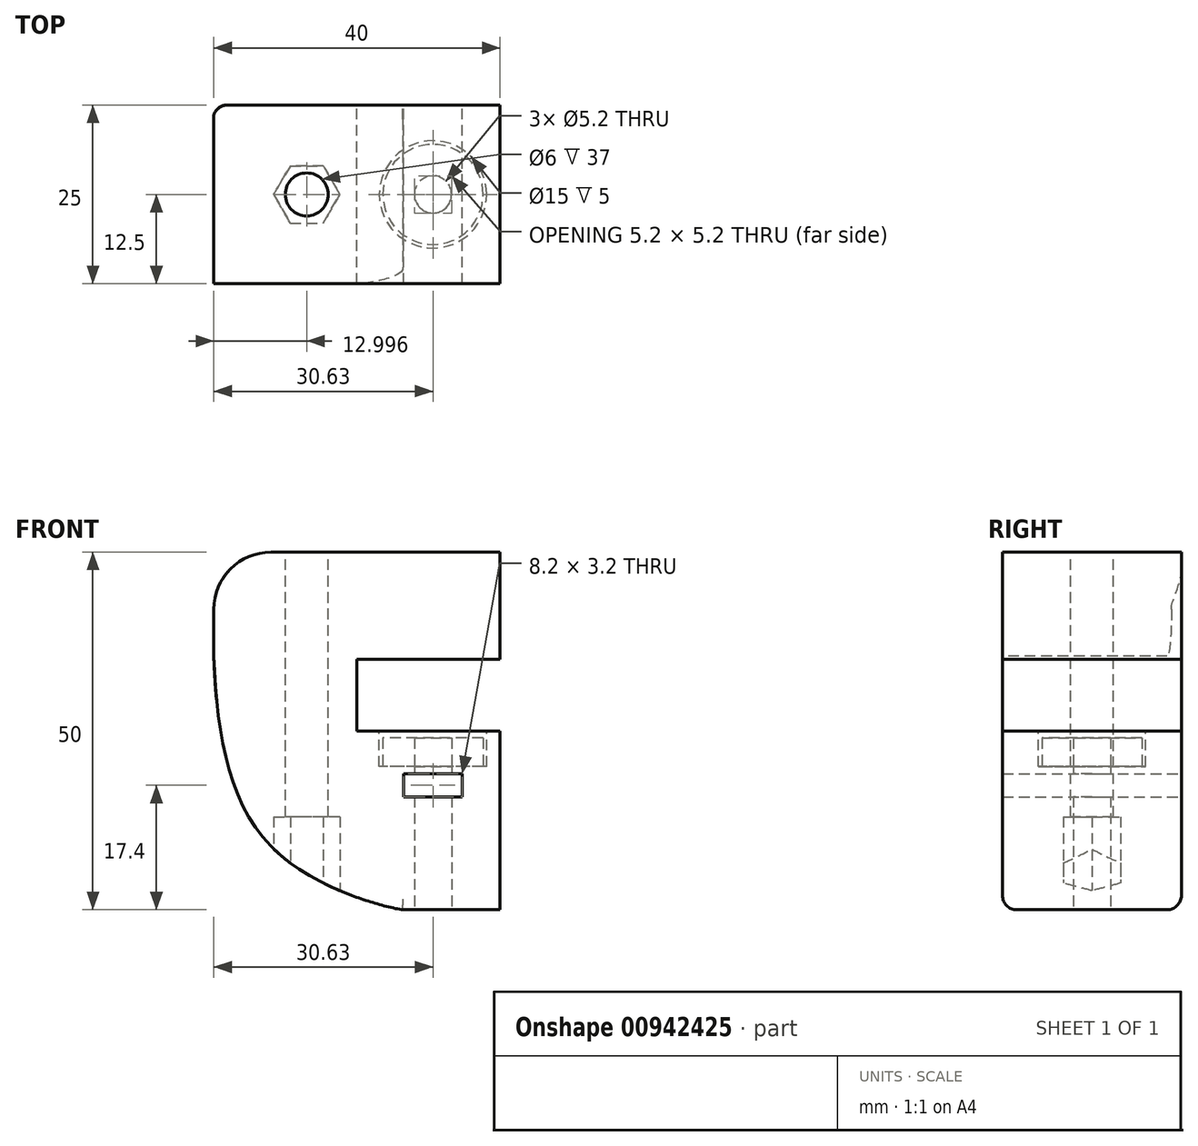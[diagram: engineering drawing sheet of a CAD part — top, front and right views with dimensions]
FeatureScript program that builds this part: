
annotation { "Feature Type Name" : "Feature", "Feature Type Description" : "" }
export const myFeature = defineFeature(function(context is Context, id is Id, definition is map)
    precondition{}
    {
        {
            var Q0;
            Q0=qCreatedBy(makeId("Front.planeOp"),FACE);
            var sketch = newSketch(context, id + "F0", { "sketchPlane" : qUnion([Q0])});
            skLineSegment(sketch, "E0", {"start": v(9.37, 10) * mm, "end": v(9.37, 25) * mm});
            skLineSegment(sketch, "E1", {"start": v(9.37, 25) * mm, "end": v(-30.63, 25) * mm});
            skLineSegment(sketch, "E2", {"start": v(-30.63, 25) * mm, "end": v(-30.63, -25) * mm});
            skLineSegment(sketch, "E3", {"start": v(9.37, -25) * mm, "end": v(9.37, 0) * mm});
            skLineSegment(sketch, "E4", {"start": v(-30.63, -25) * mm, "end": v(9.37, -25) * mm});
            skLineSegment(sketch, "E5", {"start": v(9.37, 10) * mm, "end": v(-10.63, 10) * mm});
            skLineSegment(sketch, "E6", {"start": v(-10.63, 10) * mm, "end": v(-10.63, 0) * mm});
            skLineSegment(sketch, "E7", {"start": v(-10.63, 0) * mm, "end": v(9.37, 0) * mm});
            skLineSegment(sketch, "E8.bottom", {"start": v(-4.1, -6) * mm, "end": v(4.1, -6) * mm});
            skLineSegment(sketch, "E8.top", {"start": v(-4.1, -9.2) * mm, "end": v(4.1, -9.2) * mm});
            skLineSegment(sketch, "E8.left", {"start": v(-4.1, -6) * mm, "end": v(-4.1, -9.2) * mm});
            skLineSegment(sketch, "E8.right", {"start": v(4.1, -6) * mm, "end": v(4.1, -9.2) * mm});
            skFitSpline(sketch, "E9", {"points": [v(-25, 25) * mm, v(-21.25, -15.4) * mm, v(9.37, -19.87) * mm], "startDerivative": vector(2.03, -83.34) * mm, "endDerivative": vector(87.72, 0.68) * mm});
            skSolve(sketch);
        }
        {
            var Q0;
            Q0=qSketchRegion(id+"F0",true);
            extrude(context, id + "F1", {"entities" : qUnion([Q0]), "depth" : 25 * mm, "offsetDistance" : 25 * mm});
        }
        {
            var Q0;
            Q0=makeQuery(id+"F1.opExtrude","SWEPT_FACE",FACE,{"disambiguationData":[OSD([sQuery(id+"F0.wireOp",EDGE,"E1")])]});
            var sketch = newSketch(context, id + "F2", { "sketchPlane" : qUnion([Q0])});
            skCircle(sketch, "E10", {"center": v(-17.63, -12.5) * mm, "radius": 3 * mm});
            skPoint(sketch, "E10.centerSnap0", {"position": v(-10.63, 0) * mm});
            skPoint(sketch, "E10.centerSnap1", {"position": v(-30.63, -12.5) * mm});
            skSolve(sketch);
        }
        {
            var Q0;
            Q0=makeQuery(id+"F2.imprint","IMPRINT",FACE,{"disambiguationData":[TD([[makeQuery(id+"F2.imprint","IMPRINT",EDGE,{"derivedFrom":sQuery(id+"F2.wireOp",EDGE,"E10")}),1.0]])]});
            extrude(context, id + "F3", {"entities" : qUnion([Q0]), "operationType" : NewBodyOperationType.REMOVE, "oppositeDirection" : true, "depth" : 56.7 * mm, "offsetDistance" : 25 * mm});
        }
        {
            var Q0;
            Q0=makeQuery(id+"F1.opExtrude","SWEPT_FACE",FACE,{"disambiguationData":[OSD([sQuery(id+"F0.wireOp",EDGE,"E4")])]});
            var sketch = newSketch(context, id + "F4", { "sketchPlane" : qUnion([Q0])});
            skLineSegment(sketch, "E11", {"start": v(23.4, 12.5) * mm, "end": v(-73.54, 12.5) * mm, "construction": true});
            skLineSegment(sketch, "E12.0", {"start": v(-10.63, 25) * mm, "end": v(-10.63, 0) * mm, "construction": true});
            skCircle(sketch, "E13", {"center": v(0, 12.5) * mm, "radius": 2.6 * mm});
            skSolve(sketch);
        }
        {
            var Q0;
            Q0=makeQuery(id+"F4.imprint","IMPRINT",FACE,{"disambiguationData":[TD([[makeQuery(id+"F4.imprint","IMPRINT",EDGE,{"derivedFrom":sQuery(id+"F4.wireOp",EDGE,"E13")}),1.0]])]});
            extrude(context, id + "F5", {"entities" : qUnion([Q0]), "operationType" : NewBodyOperationType.REMOVE, "oppositeDirection" : true, "depth" : 25 * mm, "offsetDistance" : 25 * mm});
        }
        {
            var Q0;
            Q0=makeQuery(id+"F1.opExtrude","SWEPT_FACE",FACE,{"disambiguationData":[OSD([sQuery(id+"F0.wireOp",EDGE,"E7")])]});
            var sketch = newSketch(context, id + "F6", { "sketchPlane" : qUnion([Q0])});
            skCircle(sketch, "E14", {"center": v(0, -12.5) * mm, "radius": 7.5 * mm});
            skSolve(sketch);
        }
        {
            var Q0;
            Q0=makeQuery(id+"F6.imprint","IMPRINT",FACE,{"disambiguationData":[TD([[makeQuery(id+"F6.imprint","IMPRINT",EDGE,{"derivedFrom":sQuery(id+"F6.wireOp",EDGE,"E14")}),1.0]])]});
            extrude(context, id + "F7", {"entities" : qUnion([Q0]), "operationType" : NewBodyOperationType.REMOVE, "oppositeDirection" : true, "depth" : 5 * mm, "offsetDistance" : 25 * mm});
        }
        {
            var Q0;
            Q0=makeQuery(id+"F1.opExtrude","SWEPT_FACE",FACE,{"disambiguationData":[OSD([sQuery(id+"F0.wireOp",EDGE,"E4")])]});
            var sketch = newSketch(context, id + "F8", { "sketchPlane" : qUnion([Q0])});
            skSolve(sketch);
        }
        {
            var Q0;
            {var subQ0=sQuery(id+"F0.wireOp",EDGE,"E4");Q0=makeQuery(id+"F8.imprint","IMPRINT",FACE,{"disambiguationData":[TD([[makeQuery(id+"F8.imprint","IMPRINT",EDGE,{"derivedFrom":makeQuery(id+"F1.opExtrude","CAP_EDGE",EDGE,{"disambiguationData":[OSD([subQ0])],"isStart":true})}),1.0]])]});}
            var sketch = newSketch(context, id + "F9", { "sketchPlane" : qUnion([Q0])});
            skCircle(sketch, "E15.0", {"center": v(-17.63, 12.5) * mm, "radius": 3 * mm, "construction": true});
            skCircle(sketch, "E16.cCircle", {"center": v(-17.63, 12.5) * mm, "radius": 4 * mm, "construction": true});
            skLineSegment(sketch, "E16.0", {"start": v(-15.32, 8.5) * mm, "end": v(-19.94, 8.5) * mm});
            skLineSegment(sketch, "E16.1", {"start": v(-19.94, 8.5) * mm, "end": v(-22.25, 12.5) * mm});
            skLineSegment(sketch, "E16.2", {"start": v(-22.25, 12.5) * mm, "end": v(-19.94, 16.5) * mm});
            skLineSegment(sketch, "E16.3", {"start": v(-19.94, 16.5) * mm, "end": v(-15.32, 16.5) * mm});
            skLineSegment(sketch, "E16.4", {"start": v(-15.32, 16.5) * mm, "end": v(-13.02, 12.5) * mm});
            skLineSegment(sketch, "E16.5", {"start": v(-13.02, 12.5) * mm, "end": v(-15.32, 8.5) * mm});
            skPoint(sketch, "E16.0.midPoint", {"position": v(-17.63, 8.5) * mm});
            skSolve(sketch);
        }
        {
            var Q0;
            Q0=makeQuery(id+"F9.imprint","IMPRINT",FACE,{"disambiguationData":[TD([[makeQuery(id+"F9.imprint","IMPRINT",EDGE,{"derivedFrom":sQuery(id+"F9.wireOp",EDGE,"E16.0")}),-1.0]])]});
            extrude(context, id + "F10", {"entities" : qUnion([Q0]), "operationType" : NewBodyOperationType.REMOVE, "oppositeDirection" : true, "depth" : 13 * mm, "offsetDistance" : 25 * mm});
        }
        {
            var Q0;
            Q0=makeQuery(id+"F1.opExtrude","CAP_FACE",FACE,{"disambiguationData":[OSD([sQuery(id+"F0.wireOp",EDGE,"E0"),sQuery(id+"F0.wireOp",EDGE,"E1"),sQuery(id+"F0.wireOp",EDGE,"E2"),sQuery(id+"F0.wireOp",EDGE,"E3"),sQuery(id+"F0.wireOp",EDGE,"E4"),sQuery(id+"F0.wireOp",EDGE,"E5"),sQuery(id+"F0.wireOp",EDGE,"E6"),sQuery(id+"F0.wireOp",EDGE,"E7"),sQuery(id+"F0.wireOp",EDGE,"E8.bottom"),sQuery(id+"F0.wireOp",EDGE,"E8.top"),sQuery(id+"F0.wireOp",EDGE,"E8.left"),sQuery(id+"F0.wireOp",EDGE,"E8.right")])],"isStart":false});
            var sketch = newSketch(context, id + "F11", { "sketchPlane" : qUnion([Q0])});
            skFitSpline(sketch, "E17", {"points": [v(-30.63, 25) * mm, v(-22.39, -16.37) * mm, v(-4.24, -25) * mm, v(-3.87, -25) * mm], "startDerivative": vector(-1.47, -87.32) * mm, "endDerivative": vector(3.99, 0.77) * mm});
            skSolve(sketch);
        }
        {
            var Q0;
            {var subQ0=sQuery(id+"F11.wireOp",EDGE,"E17");var subQ1=makeQuery(id+"F1.opExtrude","CAP_EDGE",EDGE,{"disambiguationData":[OSD([sQuery(id+"F0.wireOp",EDGE,"E2")])],"isStart":false});var subQ2=makeQuery(id+"F11.imprint","INTERSECT",VERTEX,{"derivedFrom":[subQ1,subQ0]});Q0=makeQuery(id+"F11.imprint","IMPRINT",FACE,{"disambiguationData":[TD([[makeQuery(id+"F11.imprint","IMPRINT",EDGE,{"disambiguationData":[TD([[subQ2,-1.0]])],"derivedFrom":subQ0}),-1.0]])]});}
            extrude(context, id + "F12", {"entities" : qUnion([Q0]), "operationType" : NewBodyOperationType.REMOVE, "oppositeDirection" : true, "depth" : 29.7 * mm, "offsetDistance" : 25 * mm});
        }
        {
            var Q0;
            Q0=makeQuery(id+"F1.opExtrude","CAP_EDGE",EDGE,{"disambiguationData":[OSD([sQuery(id+"F0.wireOp",EDGE,"E4")])],"isStart":false});
            var Q1;
            Q1=makeQuery(id+"F1.opExtrude","CAP_EDGE",EDGE,{"disambiguationData":[OSD([sQuery(id+"F0.wireOp",EDGE,"E4")])],"isStart":true});
            var Q2;
            Q2=makeQuery(id+"F12.boolean.opBoolean","COPY",EDGE,{"derivedFrom":makeQuery(id+"F12.opExtrude","CAP_EDGE",EDGE,{"disambiguationData":[OSD([sQuery(id+"F11.wireOp",EDGE,"E17")])],"isStart":true})});
            var Q3;
            Q3=makeQuery(id+"F12.boolean.opBoolean","INTERSECT",EDGE,{"derivedFrom":[makeQuery(id+"F1.opExtrude","CAP_FACE",FACE,{"disambiguationData":[OSD([sQuery(id+"F0.wireOp",EDGE,"E0"),sQuery(id+"F0.wireOp",EDGE,"E1"),sQuery(id+"F0.wireOp",EDGE,"E2"),sQuery(id+"F0.wireOp",EDGE,"E3"),sQuery(id+"F0.wireOp",EDGE,"E4"),sQuery(id+"F0.wireOp",EDGE,"E5"),sQuery(id+"F0.wireOp",EDGE,"E6"),sQuery(id+"F0.wireOp",EDGE,"E7"),sQuery(id+"F0.wireOp",EDGE,"E8.bottom"),sQuery(id+"F0.wireOp",EDGE,"E8.top"),sQuery(id+"F0.wireOp",EDGE,"E8.left"),sQuery(id+"F0.wireOp",EDGE,"E8.right")])],"isStart":true}),makeQuery(id+"F12.opExtrude","SWEPT_FACE",FACE,{"disambiguationData":[OSD([sQuery(id+"F11.wireOp",EDGE,"E17")])]})]});
            fillet(context, id + "F13", {"entities" : qUnion([Q0, Q1, Q2, Q3]), "radius" : 2 * mm, "tangentPropagation" : true, "allowEdgeOverflow" : false});
        }
        {
            var Q0;
            Q0=makeQuery(id+"F1.opExtrude","SWEPT_EDGE",EDGE,{"disambiguationData":[OSD([sQuery(id+"F0.wireOp",EDGE,"E1"),sQuery(id+"F0.wireOp",EDGE,"E2")])]});
            fillet(context, id + "F14", {"entities" : qUnion([Q0]), "radius" : 8 * mm, "tangentPropagation" : true, "allowEdgeOverflow" : false});
        }
        {
            var Q0;
            Q0=makeQuery(id+"F7.boolean.opBoolean","COPY",FACE,{"derivedFrom":makeQuery(id+"F7.opExtrude","CAP_FACE",FACE,{"disambiguationData":[OSD([sQuery(id+"F4.wireOp",EDGE,"E13"),sQuery(id+"F6.wireOp",EDGE,"E14")])],"isStart":false})});
            var sketch = newSketch(context, id + "F15", { "sketchPlane" : qUnion([Q0])});
            skCircle(sketch, "E18", {"center": v(0, -12.5) * mm, "radius": 7 * mm});
            skSolve(sketch);
        }
        {
            var Q0;
            Q0=makeQuery(id+"F15.imprint","IMPRINT",FACE,{"disambiguationData":[TD([[makeQuery(id+"F15.imprint","IMPRINT",EDGE,{"derivedFrom":makeQuery(id+"F7.boolean.opBoolean","COPY",EDGE,{"derivedFrom":makeQuery(id+"F7.opExtrude","CAP_EDGE",EDGE,{"disambiguationData":[OSD([sQuery(id+"F4.wireOp",EDGE,"E13")])],"isStart":false})})}),-1.0]])]});
            var Q1;
            Q1=makeQuery(id+"F15.imprint","IMPRINT",FACE,{"disambiguationData":[TD([[makeQuery(id+"F15.imprint","IMPRINT",EDGE,{"derivedFrom":sQuery(id+"F15.wireOp",EDGE,"E18")}),1.0]])]});
            extrude(context, id + "F16", {"entities" : qUnion([Q0, Q1]), "depth" : 4 * mm, "offsetDistance" : 25 * mm});
        }
    });
